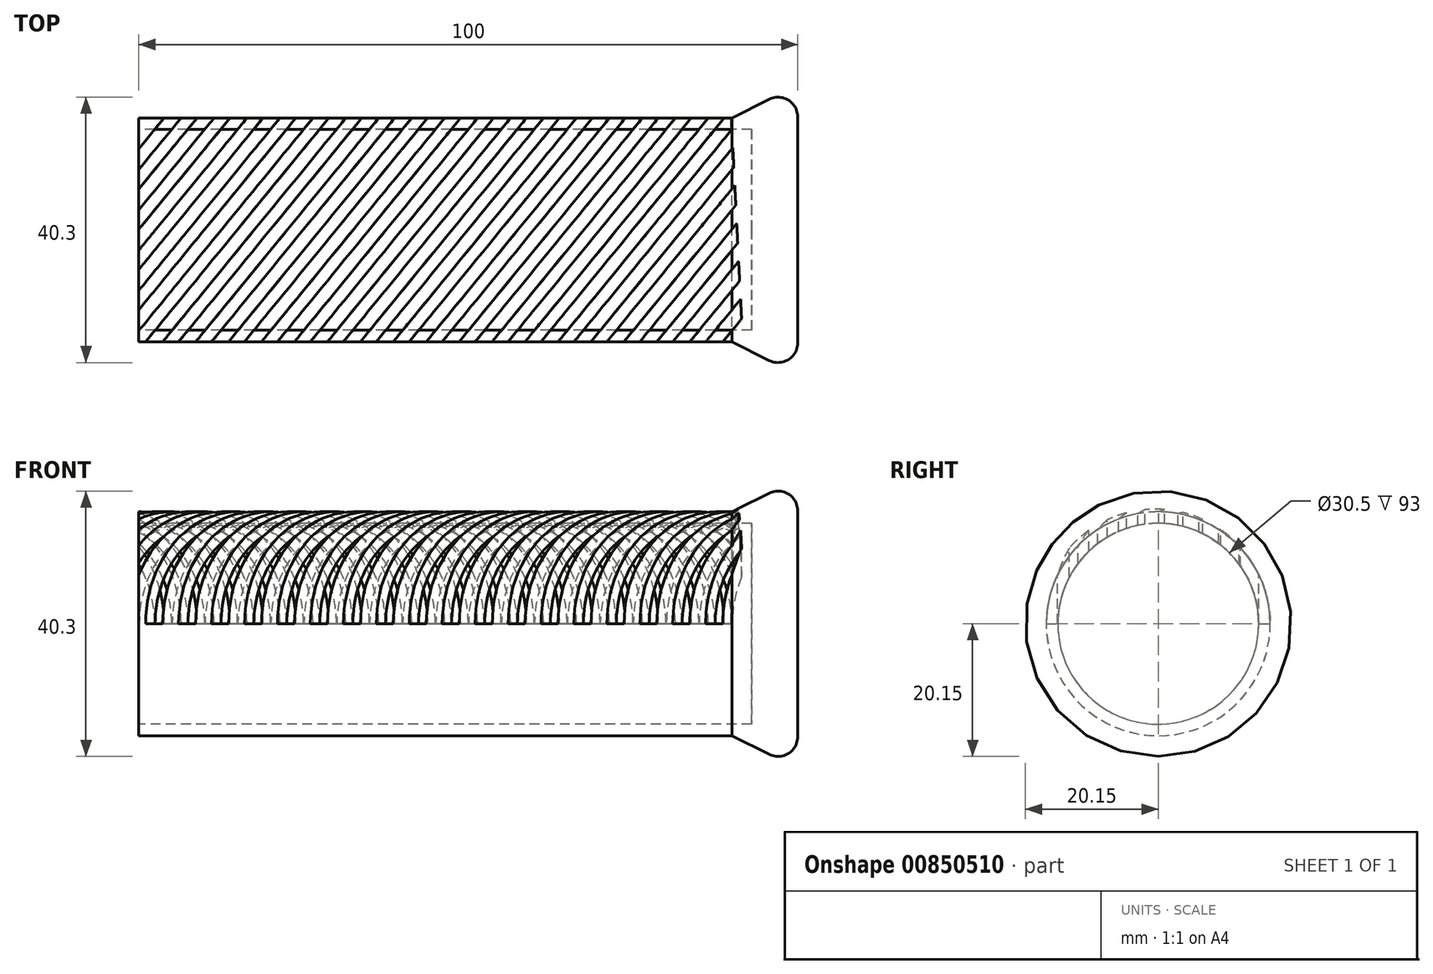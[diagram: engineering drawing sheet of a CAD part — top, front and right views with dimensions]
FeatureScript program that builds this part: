
annotation { "Feature Type Name" : "Feature", "Feature Type Description" : "" }
export const myFeature = defineFeature(function(context is Context, id is Id, definition is map)
    precondition{}
    {
        {
            var Q0;
            Q0=qCreatedBy(makeId("Right.planeOp"),FACE);
            var sketch = newSketch(context, id + "F0", { "sketchPlane" : qUnion([Q0])});
            skCircle(sketch, "E0", {"center": v(0, 0) * mm, "radius": 17 * mm});
            skSolve(sketch);
        }
        {
            var Q0;
            Q0=makeQuery(id+"F0.imprint","IMPRINT",FACE,{"disambiguationData":[TD([[makeQuery(id+"F0.imprint","IMPRINT",EDGE,{"derivedFrom":sQuery(id+"F0.wireOp",EDGE,"E0")}),1.0]])]});
            extrude(context, id + "F1", {"entities" : qUnion([Q0]), "depth" : 90 * mm, "offsetDistance" : 25 * mm});
        }
        {
            var Q0;
            Q0=makeQuery(id+"F1.opExtrude","CAP_FACE",FACE,{"disambiguationData":[OSD([sQuery(id+"F0.wireOp",EDGE,"E0")])],"isStart":false});
            cPlane(context, id + "F2", {"entities" : qUnion([Q0]), "cplaneType" : CPlaneType.OFFSET, "offset" : 10 * mm, "width" : 150 * mm, "height" : 150 * mm});
        }
        {
            var Q0;
            Q0=qCreatedBy(id+"F2.planeOp",FACE);
            var sketch = newSketch(context, id + "F3", { "sketchPlane" : qUnion([Q0])});
            skCircle(sketch, "E1", {"center": v(0, 0) * mm, "radius": 22 * mm});
            skSolve(sketch);
        }
        {
            var Q1;
            Q1=makeQuery(id+"F3.imprint","IMPRINT",FACE,{"disambiguationData":[TD([[makeQuery(id+"F3.imprint","IMPRINT",EDGE,{"derivedFrom":sQuery(id+"F3.wireOp",EDGE,"E1")}),1.0]])]});
            var Q2;
            Q2=makeQuery(id+"F1.opExtrude","CAP_FACE",FACE,{"disambiguationData":[OSD([sQuery(id+"F0.wireOp",EDGE,"E0")])],"isStart":false});
            loft(context, id + "F4", {"operationType" : NewBodyOperationType.ADD, "sheetProfilesArray" : [{ "sheetProfileEntities" : qUnion([Q1]) }, { "sheetProfileEntities" : qUnion([Q2]) }]});
        }
        {
            var Q0;
            Q0=makeQuery(id+"F4.opLoft","MID_CAP_EDGE",EDGE,{"disambiguationData":[OSD([sQuery(id+"F3.wireOp",EDGE,"E1")])],"capPos":0.0});
            fillet(context, id + "F5", {"entities" : qUnion([Q0]), "radius" : 3 * mm, "tangentPropagation" : true, "allowEdgeOverflow" : false});
        }
        {
            var Q0;
            Q0=qCreatedBy(makeId("Right.planeOp"),FACE);
            var sketch = newSketch(context, id + "F6", { "sketchPlane" : qUnion([Q0])});
            skCircle(sketch, "E2", {"center": v(0, 0) * mm, "radius": 15.17 * mm});
            skSolve(sketch);
        }
        {
            var Q0;
            Q0=makeQuery(id+"F6.imprint","IMPRINT",FACE,{"disambiguationData":[TD([[makeQuery(id+"F6.imprint","IMPRINT",EDGE,{"derivedFrom":sQuery(id+"F6.wireOp",EDGE,"E2")}),1.0]])]});
            var Q1;
            Q1=sQuery(id+"F6.wireOp",EDGE,"E2");
            extrude(context, id + "F7", {"entities" : qUnion([Q0]), "bodyType" : ToolBodyType.SURFACE, "surfaceEntities" : qUnion([Q1]), "depth" : 90 * mm, "offsetDistance" : 25 * mm});
        }
        {
            var Q0;
            Q0=qCreatedBy(makeId("Top.planeOp"),FACE);
            cPlane(context, id + "F8", {"entities" : qUnion([Q0]), "cplaneType" : CPlaneType.OFFSET, "offset" : 25 * mm, "width" : 150 * mm, "height" : 150 * mm});
        }
        {
            var Q0;
            Q0=qCreatedBy(id+"F8.planeOp",FACE);
            var sketch = newSketch(context, id + "F9", { "sketchPlane" : qUnion([Q0])});
            skLineSegment(sketch, "E3", {"start": v(0, -18.26) * mm, "end": v(34.34, 23.72) * mm});
            skLineSegment(sketch, "E4.0", {"start": v(2.57, -18.27) * mm, "end": v(37.19, 24.04) * mm});
            skLineSegment(sketch, "E5", {"start": v(0, -18.26) * mm, "end": v(2.57, -18.27) * mm});
            skLineSegment(sketch, "E6", {"start": v(34.34, 23.72) * mm, "end": v(37.19, 24.04) * mm});
            skLineSegment(sketch, "E7.1.0.0", {"start": v(5, -18.26) * mm, "end": v(39.34, 23.72) * mm});
            skLineSegment(sketch, "E7.1.0.1", {"start": v(7.57, -18.27) * mm, "end": v(42.19, 24.04) * mm});
            skLineSegment(sketch, "E7.1.0.2", {"start": v(5, -18.26) * mm, "end": v(7.57, -18.27) * mm});
            skLineSegment(sketch, "E7.1.0.3", {"start": v(39.34, 23.72) * mm, "end": v(42.19, 24.04) * mm});
            skLineSegment(sketch, "E7.2.0.0", {"start": v(10, -18.26) * mm, "end": v(44.34, 23.72) * mm});
            skLineSegment(sketch, "E7.2.0.1", {"start": v(12.57, -18.27) * mm, "end": v(47.19, 24.04) * mm});
            skLineSegment(sketch, "E7.2.0.2", {"start": v(10, -18.26) * mm, "end": v(12.57, -18.27) * mm});
            skLineSegment(sketch, "E7.2.0.3", {"start": v(44.34, 23.72) * mm, "end": v(47.19, 24.04) * mm});
            skLineSegment(sketch, "E7.3.0.0", {"start": v(15, -18.26) * mm, "end": v(49.34, 23.72) * mm});
            skLineSegment(sketch, "E7.3.0.1", {"start": v(17.57, -18.27) * mm, "end": v(52.19, 24.04) * mm});
            skLineSegment(sketch, "E7.3.0.2", {"start": v(15, -18.26) * mm, "end": v(17.57, -18.27) * mm});
            skLineSegment(sketch, "E7.3.0.3", {"start": v(49.34, 23.72) * mm, "end": v(52.19, 24.04) * mm});
            skLineSegment(sketch, "E7.4.0.0", {"start": v(20, -18.26) * mm, "end": v(54.34, 23.72) * mm});
            skLineSegment(sketch, "E7.4.0.1", {"start": v(22.57, -18.27) * mm, "end": v(57.19, 24.04) * mm});
            skLineSegment(sketch, "E7.4.0.2", {"start": v(20, -18.26) * mm, "end": v(22.57, -18.27) * mm});
            skLineSegment(sketch, "E7.4.0.3", {"start": v(54.34, 23.72) * mm, "end": v(57.19, 24.04) * mm});
            skLineSegment(sketch, "E7.5.0.0", {"start": v(25, -18.26) * mm, "end": v(59.34, 23.72) * mm});
            skLineSegment(sketch, "E7.5.0.1", {"start": v(27.57, -18.27) * mm, "end": v(62.19, 24.04) * mm});
            skLineSegment(sketch, "E7.5.0.2", {"start": v(25, -18.26) * mm, "end": v(27.57, -18.27) * mm});
            skLineSegment(sketch, "E7.5.0.3", {"start": v(59.34, 23.72) * mm, "end": v(62.19, 24.04) * mm});
            skLineSegment(sketch, "E7.6.0.0", {"start": v(30, -18.26) * mm, "end": v(64.34, 23.72) * mm});
            skLineSegment(sketch, "E7.6.0.1", {"start": v(32.57, -18.27) * mm, "end": v(67.19, 24.04) * mm});
            skLineSegment(sketch, "E7.6.0.2", {"start": v(30, -18.26) * mm, "end": v(32.57, -18.27) * mm});
            skLineSegment(sketch, "E7.6.0.3", {"start": v(64.34, 23.72) * mm, "end": v(67.19, 24.04) * mm});
            skLineSegment(sketch, "E7.direction1", {"start": v(0, -18.26) * mm, "end": v(5, -18.26) * mm, "construction": true});
            skLineSegment(sketch, "E8.0.7.0", {"start": v(35, -18.26) * mm, "end": v(69.34, 23.72) * mm});
            skLineSegment(sketch, "E8.3.7.0", {"start": v(37.57, -18.27) * mm, "end": v(72.19, 24.04) * mm});
            skLineSegment(sketch, "E8.6.7.0", {"start": v(35, -18.26) * mm, "end": v(37.57, -18.27) * mm});
            skLineSegment(sketch, "E8.9.7.0", {"start": v(69.34, 23.72) * mm, "end": v(72.19, 24.04) * mm});
            skLineSegment(sketch, "E8.0.8.0", {"start": v(40, -18.26) * mm, "end": v(74.34, 23.72) * mm});
            skLineSegment(sketch, "E8.3.8.0", {"start": v(42.57, -18.27) * mm, "end": v(77.19, 24.04) * mm});
            skLineSegment(sketch, "E8.6.8.0", {"start": v(40, -18.26) * mm, "end": v(42.57, -18.27) * mm});
            skLineSegment(sketch, "E8.9.8.0", {"start": v(74.34, 23.72) * mm, "end": v(77.19, 24.04) * mm});
            skLineSegment(sketch, "E8.0.9.0", {"start": v(45, -18.26) * mm, "end": v(79.34, 23.72) * mm});
            skLineSegment(sketch, "E8.3.9.0", {"start": v(47.57, -18.27) * mm, "end": v(82.19, 24.04) * mm});
            skLineSegment(sketch, "E8.6.9.0", {"start": v(45, -18.26) * mm, "end": v(47.57, -18.27) * mm});
            skLineSegment(sketch, "E8.9.9.0", {"start": v(79.34, 23.72) * mm, "end": v(82.19, 24.04) * mm});
            skLineSegment(sketch, "E8.0.10.0", {"start": v(50, -18.26) * mm, "end": v(84.34, 23.72) * mm});
            skLineSegment(sketch, "E8.3.10.0", {"start": v(52.57, -18.27) * mm, "end": v(87.19, 24.04) * mm});
            skLineSegment(sketch, "E8.6.10.0", {"start": v(50, -18.26) * mm, "end": v(52.57, -18.27) * mm});
            skLineSegment(sketch, "E8.9.10.0", {"start": v(84.34, 23.72) * mm, "end": v(87.19, 24.04) * mm});
            skLineSegment(sketch, "E8.0.11.0", {"start": v(55, -18.26) * mm, "end": v(89.34, 23.72) * mm});
            skLineSegment(sketch, "E8.3.11.0", {"start": v(57.57, -18.27) * mm, "end": v(89.71, 21.02) * mm});
            skLineSegment(sketch, "E8.6.11.0", {"start": v(55, -18.26) * mm, "end": v(57.57, -18.27) * mm});
            skLineSegment(sketch, "E8.9.11.0", {"start": v(89.34, 23.72) * mm, "end": v(89.57, 23.75) * mm});
            skLineSegment(sketch, "E8.0.12.0", {"start": v(60, -18.26) * mm, "end": v(89.85, 18.24) * mm});
            skLineSegment(sketch, "E8.3.12.0", {"start": v(62.57, -18.27) * mm, "end": v(90, 15.26) * mm});
            skLineSegment(sketch, "E8.6.12.0", {"start": v(60, -18.26) * mm, "end": v(62.57, -18.27) * mm});
            skLineSegment(sketch, "E9.0.13.0", {"start": v(65, -18.26) * mm, "end": v(90.15, 12.48) * mm});
            skLineSegment(sketch, "E9.3.13.0", {"start": v(67.57, -18.27) * mm, "end": v(90.3, 9.51) * mm});
            skLineSegment(sketch, "E9.6.13.0", {"start": v(65, -18.26) * mm, "end": v(67.57, -18.27) * mm});
            skLineSegment(sketch, "E9.0.14.0", {"start": v(70, -18.26) * mm, "end": v(90.44, 6.73) * mm});
            skLineSegment(sketch, "E9.3.14.0", {"start": v(72.57, -18.27) * mm, "end": v(90.6, 3.76) * mm});
            skLineSegment(sketch, "E9.6.14.0", {"start": v(70, -18.26) * mm, "end": v(72.57, -18.27) * mm});
            skLineSegment(sketch, "E10.0.15.0", {"start": v(75, -18.26) * mm, "end": v(90.74, 0.98) * mm});
            skLineSegment(sketch, "E10.3.15.0", {"start": v(77.57, -18.27) * mm, "end": v(90.89, -2) * mm});
            skLineSegment(sketch, "E10.6.15.0", {"start": v(75, -18.26) * mm, "end": v(77.57, -18.27) * mm});
            skLineSegment(sketch, "E10.0.16.0", {"start": v(80, -18.26) * mm, "end": v(91.03, -4.78) * mm});
            skLineSegment(sketch, "E10.6.16.0", {"start": v(80, -18.26) * mm, "end": v(82.57, -18.27) * mm});
            skLineSegment(sketch, "E10.0.17.0", {"start": v(85, -18.26) * mm, "end": v(91.32, -10.53) * mm});
            skLineSegment(sketch, "E10.3.17.0", {"start": v(87.57, -18.27) * mm, "end": v(91.48, -13.5) * mm});
            skLineSegment(sketch, "E10.6.17.0", {"start": v(85, -18.26) * mm, "end": v(87.57, -18.27) * mm});
            skLineSegment(sketch, "E11", {"start": v(91.48, -13.5) * mm, "end": v(89.57, 23.75) * mm});
            skPoint(sketch, "E12.orphan", {"position": v(92.19, 24.04) * mm});
            skPoint(sketch, "E13.orphan", {"position": v(97.19, 24.04) * mm});
            skPoint(sketch, "E14.orphan", {"position": v(89.34, 28.33) * mm});
            skLineSegment(sketch, "E15", {"start": v(82.57, -18.27) * mm, "end": v(91.18, -7.75) * mm});
            skLineSegment(sketch, "E16.direction1", {"start": v(0, -18.26) * mm, "end": v(25, -18.26) * mm, "construction": true});
            skLineSegment(sketch, "E17.1.0.0", {"start": v(29.34, 23.72) * mm, "end": v(32.19, 24.04) * mm});
            skLineSegment(sketch, "E17.1.0.1", {"start": v(0, -15.3) * mm, "end": v(32.19, 24.04) * mm});
            skLineSegment(sketch, "E17.1.0.2", {"start": v(0, -12.15) * mm, "end": v(29.34, 23.72) * mm});
            skLineSegment(sketch, "E17.2.0.0", {"start": v(24.34, 23.72) * mm, "end": v(27.19, 24.04) * mm});
            skLineSegment(sketch, "E17.2.0.1", {"start": v(0, -9.2) * mm, "end": v(27.19, 24.04) * mm});
            skLineSegment(sketch, "E17.2.0.2", {"start": v(0, -6.04) * mm, "end": v(24.34, 23.72) * mm});
            skLineSegment(sketch, "E17.3.0.0", {"start": v(19.34, 23.72) * mm, "end": v(22.19, 24.04) * mm});
            skLineSegment(sketch, "E17.3.0.1", {"start": v(0, -3.08) * mm, "end": v(22.19, 24.04) * mm});
            skLineSegment(sketch, "E17.3.0.2", {"start": v(0, 0.08) * mm, "end": v(19.34, 23.72) * mm});
            skLineSegment(sketch, "E17.4.0.0", {"start": v(14.34, 23.72) * mm, "end": v(17.19, 24.04) * mm});
            skLineSegment(sketch, "E17.4.0.1", {"start": v(0, 3.03) * mm, "end": v(17.19, 24.04) * mm});
            skLineSegment(sketch, "E17.5.0.0", {"start": v(9.34, 23.72) * mm, "end": v(12.19, 24.04) * mm});
            skLineSegment(sketch, "E17.5.0.1", {"start": v(0, 9.14) * mm, "end": v(12.19, 24.04) * mm});
            skLineSegment(sketch, "E17.5.0.2", {"start": v(0, 12.3) * mm, "end": v(9.34, 23.72) * mm});
            skLineSegment(sketch, "E17.direction1", {"start": v(34.34, 23.72) * mm, "end": v(29.34, 23.72) * mm, "construction": true});
            skLineSegment(sketch, "E18", {"start": v(0, 17.03) * mm, "end": v(0, -20.32) * mm});
            skPoint(sketch, "E19.orphan", {"position": v(-2.43, -18.27) * mm});
            skLineSegment(sketch, "E20", {"start": v(14.34, 23.72) * mm, "end": v(0, 6.2) * mm});
            skSolve(sketch);
        }
        {
            var Q0;
            Q0=makeQuery(id+"F9.imprint","IMPRINT",FACE,{"disambiguationData":[TD([[makeQuery(id+"F9.imprint","IMPRINT",EDGE,{"derivedFrom":sQuery(id+"F9.wireOp",EDGE,"E17.4.0.0")}),-1.0]])]});
            var Q1;
            Q1=makeQuery(id+"F9.imprint","IMPRINT",FACE,{"disambiguationData":[TD([[makeQuery(id+"F9.imprint","IMPRINT",EDGE,{"derivedFrom":sQuery(id+"F9.wireOp",EDGE,"E17.5.0.0")}),-1.0]])]});
            var Q2;
            Q2=makeQuery(id+"F9.imprint","IMPRINT",FACE,{"disambiguationData":[TD([[makeQuery(id+"F9.imprint","IMPRINT",EDGE,{"derivedFrom":sQuery(id+"F9.wireOp",EDGE,"E17.3.0.0")}),-1.0]])]});
            var Q3;
            Q3=makeQuery(id+"F9.imprint","IMPRINT",FACE,{"disambiguationData":[TD([[makeQuery(id+"F9.imprint","IMPRINT",EDGE,{"derivedFrom":sQuery(id+"F9.wireOp",EDGE,"E17.2.0.0")}),-1.0]])]});
            var Q4;
            Q4=makeQuery(id+"F9.imprint","IMPRINT",FACE,{"disambiguationData":[TD([[makeQuery(id+"F9.imprint","IMPRINT",EDGE,{"derivedFrom":sQuery(id+"F9.wireOp",EDGE,"E17.1.0.0")}),-1.0]])]});
            var Q5;
            Q5=makeQuery(id+"F9.imprint","IMPRINT",FACE,{"disambiguationData":[TD([[makeQuery(id+"F9.imprint","IMPRINT",EDGE,{"derivedFrom":sQuery(id+"F9.wireOp",EDGE,"E7.1.0.0")}),-1.0]])]});
            var Q6;
            Q6=makeQuery(id+"F9.imprint","IMPRINT",FACE,{"disambiguationData":[TD([[makeQuery(id+"F9.imprint","IMPRINT",EDGE,{"derivedFrom":sQuery(id+"F9.wireOp",EDGE,"E7.2.0.0")}),-1.0]])]});
            var Q7;
            Q7=makeQuery(id+"F9.imprint","IMPRINT",FACE,{"disambiguationData":[TD([[makeQuery(id+"F9.imprint","IMPRINT",EDGE,{"derivedFrom":sQuery(id+"F9.wireOp",EDGE,"E7.3.0.0")}),-1.0]])]});
            var Q8;
            Q8=makeQuery(id+"F9.imprint","IMPRINT",FACE,{"disambiguationData":[TD([[makeQuery(id+"F9.imprint","IMPRINT",EDGE,{"derivedFrom":sQuery(id+"F9.wireOp",EDGE,"E7.4.0.0")}),-1.0]])]});
            var Q9;
            Q9=makeQuery(id+"F9.imprint","IMPRINT",FACE,{"disambiguationData":[TD([[makeQuery(id+"F9.imprint","IMPRINT",EDGE,{"derivedFrom":sQuery(id+"F9.wireOp",EDGE,"E7.5.0.2")}),1.0]])]});
            var Q10;
            Q10=makeQuery(id+"F9.imprint","IMPRINT",FACE,{"disambiguationData":[TD([[makeQuery(id+"F9.imprint","IMPRINT",EDGE,{"derivedFrom":sQuery(id+"F9.wireOp",EDGE,"E7.6.0.0")}),-1.0]])]});
            var Q11;
            Q11=makeQuery(id+"F9.imprint","IMPRINT",FACE,{"disambiguationData":[TD([[makeQuery(id+"F9.imprint","IMPRINT",EDGE,{"derivedFrom":sQuery(id+"F9.wireOp",EDGE,"E8.0.7.0")}),-1.0]])]});
            var Q12;
            Q12=makeQuery(id+"F9.imprint","IMPRINT",FACE,{"disambiguationData":[TD([[makeQuery(id+"F9.imprint","IMPRINT",EDGE,{"derivedFrom":sQuery(id+"F9.wireOp",EDGE,"E8.0.8.0")}),-1.0]])]});
            var Q13;
            Q13=makeQuery(id+"F9.imprint","IMPRINT",FACE,{"disambiguationData":[TD([[makeQuery(id+"F9.imprint","IMPRINT",EDGE,{"derivedFrom":sQuery(id+"F9.wireOp",EDGE,"E8.0.9.0")}),-1.0]])]});
            var Q14;
            Q14=makeQuery(id+"F9.imprint","IMPRINT",FACE,{"disambiguationData":[TD([[makeQuery(id+"F9.imprint","IMPRINT",EDGE,{"derivedFrom":sQuery(id+"F9.wireOp",EDGE,"E8.6.10.0")}),1.0]])]});
            var Q15;
            Q15=makeQuery(id+"F9.imprint","IMPRINT",FACE,{"disambiguationData":[TD([[makeQuery(id+"F9.imprint","IMPRINT",EDGE,{"derivedFrom":sQuery(id+"F9.wireOp",EDGE,"E8.0.11.0")}),-1.0]])]});
            var Q16;
            {var subQ0=sQuery(id+"F9.wireOp",EDGE,"E8.0.12.0");Q16=makeQuery(id+"F9.imprint","IMPRINT",FACE,{"disambiguationData":[TD([[makeQuery(id+"F9.imprint","IMPRINT",EDGE,{"derivedFrom":subQ0}),-1.0]])]});}
            var Q17;
            {var subQ0=sQuery(id+"F9.wireOp",EDGE,"E9.0.13.0");Q17=makeQuery(id+"F9.imprint","IMPRINT",FACE,{"disambiguationData":[TD([[makeQuery(id+"F9.imprint","IMPRINT",EDGE,{"derivedFrom":subQ0}),-1.0]])]});}
            var Q18;
            {var subQ0=sQuery(id+"F9.wireOp",EDGE,"E9.0.14.0");Q18=makeQuery(id+"F9.imprint","IMPRINT",FACE,{"disambiguationData":[TD([[makeQuery(id+"F9.imprint","IMPRINT",EDGE,{"derivedFrom":subQ0}),-1.0]])]});}
            var Q19;
            {var subQ0=sQuery(id+"F9.wireOp",EDGE,"E10.0.15.0");Q19=makeQuery(id+"F9.imprint","IMPRINT",FACE,{"disambiguationData":[TD([[makeQuery(id+"F9.imprint","IMPRINT",EDGE,{"derivedFrom":subQ0}),-1.0]])]});}
            var Q20;
            {var subQ0=sQuery(id+"F9.wireOp",EDGE,"E10.0.16.0");Q20=makeQuery(id+"F9.imprint","IMPRINT",FACE,{"disambiguationData":[TD([[makeQuery(id+"F9.imprint","IMPRINT",EDGE,{"derivedFrom":subQ0}),-1.0]])]});}
            var Q21;
            {var subQ0=sQuery(id+"F9.wireOp",EDGE,"E10.0.17.0");Q21=makeQuery(id+"F9.imprint","IMPRINT",FACE,{"disambiguationData":[TD([[makeQuery(id+"F9.imprint","IMPRINT",EDGE,{"derivedFrom":subQ0}),-1.0]])]});}
            var Q22;
            Q22=makeQuery(id+"F9.imprint","IMPRINT",FACE,{"disambiguationData":[TD([[makeQuery(id+"F9.imprint","IMPRINT",EDGE,{"derivedFrom":sQuery(id+"F9.wireOp",EDGE,"E3")}),-1.0]])]});
            extrude(context, id + "F10", {"entities" : qUnion([Q0, Q1, Q2, Q3, Q4, Q5, Q6, Q7, Q8, Q9, Q10, Q11, Q12, Q13, Q14, Q15, Q16, Q17, Q18, Q19, Q20, Q21, Q22]), "operationType" : NewBodyOperationType.REMOVE, "oppositeDirection" : true, "depth" : 25 * mm, "offsetDistance" : 25 * mm});
        }
        {
            var Q0;
            Q0=qCreatedBy(makeId("Right.planeOp"),FACE);
            var sketch = newSketch(context, id + "F11", { "sketchPlane" : qUnion([Q0])});
            skCircle(sketch, "E21", {"center": v(0, 0) * mm, "radius": 15.25 * mm});
            skSolve(sketch);
        }
        {
            var Q0;
            Q0=makeQuery(id+"F11.imprint","IMPRINT",FACE,{"disambiguationData":[TD([[makeQuery(id+"F11.imprint","IMPRINT",EDGE,{"derivedFrom":sQuery(id+"F11.wireOp",EDGE,"E21")}),1.0]])]});
            var Q1;
            Q1=sQuery(id+"F11.wireOp",EDGE,"E21");
            extrude(context, id + "F12", {"entities" : qUnion([Q0]), "operationType" : NewBodyOperationType.REMOVE, "surfaceEntities" : qUnion([Q1]), "depth" : 93 * mm, "offsetDistance" : 25 * mm});
        }
    });
